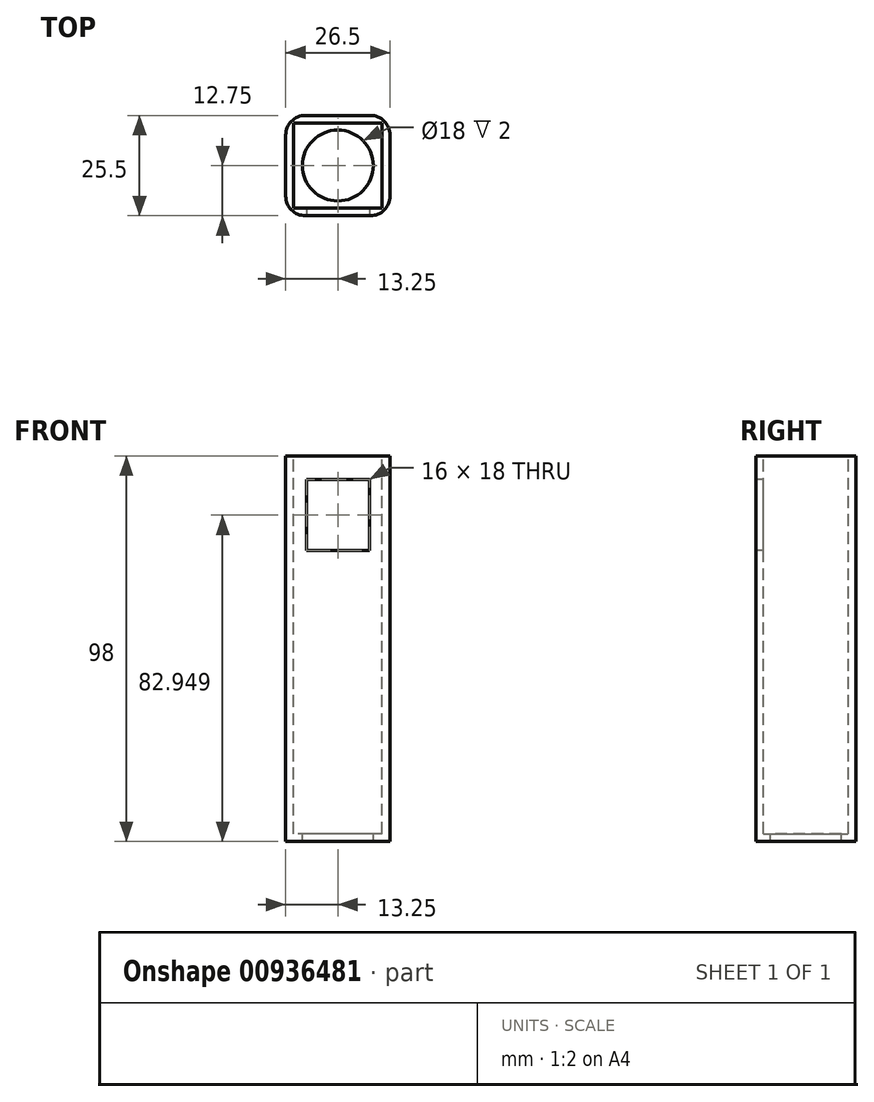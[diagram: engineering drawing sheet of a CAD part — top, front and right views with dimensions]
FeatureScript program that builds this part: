
annotation { "Feature Type Name" : "Feature", "Feature Type Description" : "" }
export const myFeature = defineFeature(function(context is Context, id is Id, definition is map)
    precondition{}
    {
        {
            var Q0;
            Q0=qCreatedBy(makeId("Top.planeOp"),FACE);
            var sketch = newSketch(context, id + "F0", { "sketchPlane" : qUnion([Q0])});
            skLineSegment(sketch, "E0.bottom", {"start": v(13.25, -12.75) * mm, "end": v(-13.25, -12.75) * mm});
            skLineSegment(sketch, "E0.top", {"start": v(13.25, 12.75) * mm, "end": v(-13.25, 12.75) * mm});
            skLineSegment(sketch, "E0.left", {"start": v(13.25, -12.75) * mm, "end": v(13.25, 12.75) * mm});
            skLineSegment(sketch, "E0.right", {"start": v(-13.25, -12.75) * mm, "end": v(-13.25, 12.75) * mm});
            skPoint(sketch, "E0.middle", {"position": v(0, 0) * mm});
            skSolve(sketch);
        }
        {
            var Q0;
            Q0=makeQuery(id+"F0.imprint","IMPRINT",FACE,{"disambiguationData":[TD([[makeQuery(id+"F0.imprint","IMPRINT",EDGE,{"derivedFrom":sQuery(id+"F0.wireOp",EDGE,"E0.bottom")}),-1.0]])]});
            extrude(context, id + "F1", {"entities" : qUnion([Q0]), "oppositeDirection" : true, "depth" : 98 * mm, "offsetDistance" : 25 * mm});
        }
        {
            var Q0;
            Q0=makeQuery(id+"F1.opExtrude","CAP_FACE",FACE,{"disambiguationData":[OSD([sQuery(id+"F0.wireOp",EDGE,"E0.bottom"),sQuery(id+"F0.wireOp",EDGE,"E0.top"),sQuery(id+"F0.wireOp",EDGE,"E0.left"),sQuery(id+"F0.wireOp",EDGE,"E0.right")])],"isStart":true});
            shell(context, id + "F2", {"entities" : qUnion([Q0]), "thickness" : 2 * mm});
        }
        {
            var Q0;
            Q0=qCreatedBy(makeId("Top.planeOp"),FACE);
            var sketch = newSketch(context, id + "F3", { "sketchPlane" : qUnion([Q0])});
            skCircle(sketch, "E1", {"center": v(0, 0) * mm, "radius": 9 * mm});
            skSolve(sketch);
        }
        {
            var Q0;
            Q0=sQuery(id+"F3.wireOp",VERTEX,"E1.center");
            var Q1;
            Q1=makeQuery(id+"F1.opExtrude","SWEPT_BODY",BODY,{"disambiguationData":[OSD([sQuery(id+"F0.wireOp",EDGE,"E0.bottom"),sQuery(id+"F0.wireOp",EDGE,"E0.top"),sQuery(id+"F0.wireOp",EDGE,"E0.left"),sQuery(id+"F0.wireOp",EDGE,"E0.right")])]});
            hole(context, id + "F4", {"style" : HoleStyle.SIMPLE, "endStyle" : HoleEndStyle.THROUGH, "holeDiameter" : 18 * mm, "majorDiameter" : 5 * mm, "isTappedThrough" : true, "tappedDepth" : 12 * mm, "tapClearance" : 3, "locations" : qUnion([Q0]), "scope" : qUnion([Q1])});
        }
        {
            var Q0;
            Q0=makeQuery(id+"F1.opExtrude","SWEPT_FACE",FACE,{"disambiguationData":[OSD([sQuery(id+"F0.wireOp",EDGE,"E0.bottom")])]});
            var sketch = newSketch(context, id + "F5", { "sketchPlane" : qUnion([Q0])});
            skLineSegment(sketch, "E2.bottom", {"start": v(8, -24.05) * mm, "end": v(-8, -24.05) * mm});
            skLineSegment(sketch, "E2.top", {"start": v(8, -6.05) * mm, "end": v(-8, -6.05) * mm});
            skLineSegment(sketch, "E2.left", {"start": v(8, -24.05) * mm, "end": v(8, -6.05) * mm});
            skLineSegment(sketch, "E2.right", {"start": v(-8, -24.05) * mm, "end": v(-8, -6.05) * mm});
            skPoint(sketch, "E2.middle", {"position": v(0, -15.05) * mm});
            skSolve(sketch);
        }
        {
            var Q0;
            Q0=makeQuery(id+"F5.imprint","IMPRINT",FACE,{"disambiguationData":[TD([[makeQuery(id+"F5.imprint","IMPRINT",EDGE,{"derivedFrom":sQuery(id+"F5.wireOp",EDGE,"E2.bottom")}),-1.0]])]});
            extrude(context, id + "F6", {"entities" : qUnion([Q0]), "operationType" : NewBodyOperationType.REMOVE, "oppositeDirection" : true, "depth" : 2 * mm, "offsetDistance" : 25 * mm});
        }
        {
            var Q0;
            Q0=makeQuery(id+"F1.opExtrude","SWEPT_EDGE",EDGE,{"disambiguationData":[OSD([sQuery(id+"F0.wireOp",EDGE,"E0.bottom"),sQuery(id+"F0.wireOp",EDGE,"E0.left")])]});
            var Q1;
            Q1=makeQuery(id+"F1.opExtrude","SWEPT_EDGE",EDGE,{"disambiguationData":[OSD([sQuery(id+"F0.wireOp",EDGE,"E0.top"),sQuery(id+"F0.wireOp",EDGE,"E0.left")])]});
            var Q2;
            Q2=makeQuery(id+"F1.opExtrude","SWEPT_EDGE",EDGE,{"disambiguationData":[OSD([sQuery(id+"F0.wireOp",EDGE,"E0.bottom"),sQuery(id+"F0.wireOp",EDGE,"E0.right")])]});
            var Q3;
            Q3=makeQuery(id+"F1.opExtrude","SWEPT_EDGE",EDGE,{"disambiguationData":[OSD([sQuery(id+"F0.wireOp",EDGE,"E0.top"),sQuery(id+"F0.wireOp",EDGE,"E0.right")])]});
            fillet(context, id + "F7", {"entities" : qUnion([Q0, Q1, Q2, Q3]), "radius" : 5 * mm, "tangentPropagation" : true, "allowEdgeOverflow" : false});
        }
    });
